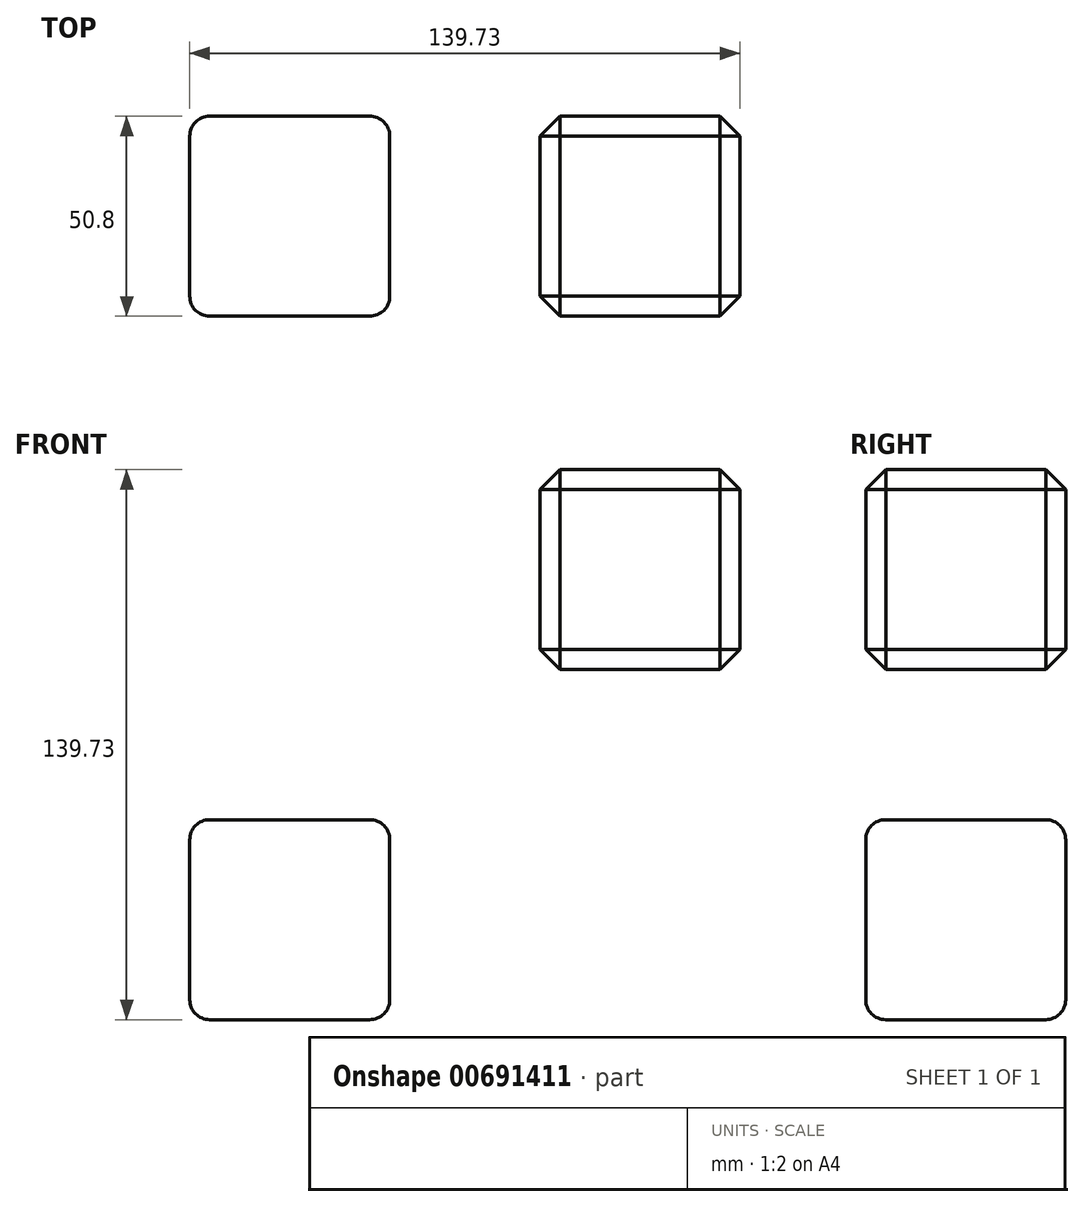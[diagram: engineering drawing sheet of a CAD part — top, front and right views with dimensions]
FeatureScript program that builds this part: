
annotation { "Feature Type Name" : "Feature", "Feature Type Description" : "" }
export const myFeature = defineFeature(function(context is Context, id is Id, definition is map)
    precondition{}
    {
        {
            var Q0;
            Q0=qCreatedBy(makeId("Front.planeOp"),FACE);
            var sketch = newSketch(context, id + "F0", { "sketchPlane" : qUnion([Q0])});
            skLineSegment(sketch, "E0.bottom", {"start": v(-25.4, 25.4) * mm, "end": v(25.4, 25.4) * mm});
            skLineSegment(sketch, "E0.top", {"start": v(-25.4, -25.4) * mm, "end": v(25.4, -25.4) * mm});
            skLineSegment(sketch, "E0.left", {"start": v(-25.4, 25.4) * mm, "end": v(-25.4, -25.4) * mm});
            skLineSegment(sketch, "E0.right", {"start": v(25.4, 25.4) * mm, "end": v(25.4, -25.4) * mm});
            skPoint(sketch, "E0.middle", {"position": v(0, 0) * mm});
            skLineSegment(sketch, "E1.bottom", {"start": v(63.53, 63.53) * mm, "end": v(114.33, 63.53) * mm});
            skLineSegment(sketch, "E1.top", {"start": v(63.53, 114.33) * mm, "end": v(114.33, 114.33) * mm});
            skLineSegment(sketch, "E1.left", {"start": v(63.53, 63.53) * mm, "end": v(63.53, 114.33) * mm});
            skLineSegment(sketch, "E1.right", {"start": v(114.33, 63.53) * mm, "end": v(114.33, 114.33) * mm});
            skLineSegment(sketch, "E2.0", {"start": v(63.53, 107.98) * mm, "end": v(38.13, 107.98) * mm});
            skArc(sketch, "E2.1", {"start": v(-19.05, 50.8) * mm, "mid": v(-2.3, 91.23) * mm, "end": v(38.13, 107.98) * mm});
            skLineSegment(sketch, "E2.2", {"start": v(-19.05, 25.4) * mm, "end": v(-19.05, 50.8) * mm});
            skLineSegment(sketch, "E3.0", {"start": v(38.13, 69.88) * mm, "end": v(63.53, 69.88) * mm});
            skArc(sketch, "E3.1", {"start": v(19.05, 50.8) * mm, "mid": v(24.64, 64.3) * mm, "end": v(38.13, 69.88) * mm});
            skLineSegment(sketch, "E3.2", {"start": v(19.05, 25.4) * mm, "end": v(19.05, 50.8) * mm});
            skSolve(sketch);
        }
        {
            var Q0;
            {var subQ3=sQuery(id+"F0.wireOp",EDGE,"E1.bottom");Q0=makeQuery(id+"F0.imprint","IMPRINT",FACE,{"disambiguationData":[TD([[makeQuery(id+"F0.imprint","IMPRINT",EDGE,{"derivedFrom":subQ3}),1.0]])]});}
            var Q1;
            Q1=makeQuery(id+"F0.imprint","IMPRINT",FACE,{"disambiguationData":[TD([[makeQuery(id+"F0.imprint","IMPRINT",EDGE,{"derivedFrom":sQuery(id+"F0.wireOp",EDGE,"E0.top")}),1.0]])]});
            extrude(context, id + "F1", {"entities" : qUnion([Q0, Q1]), "endBound" : BoundingType.SYMMETRIC, "depth" : 50.8 * mm, "offsetDistance" : 25.4 * mm});
        }
        {
            var Q0;
            Q0=makeQuery(id+"F1.opExtrude","CAP_EDGE",EDGE,{"disambiguationData":[OSD([sQuery(id+"F0.wireOp",EDGE,"E0.bottom")])],"isStart":false});
            var Q1;
            Q1=makeQuery(id+"F1.opExtrude","CAP_EDGE",EDGE,{"disambiguationData":[OSD([sQuery(id+"F0.wireOp",EDGE,"E0.right")])],"isStart":false});
            var Q2;
            Q2=makeQuery(id+"F1.opExtrude","SWEPT_EDGE",EDGE,{"disambiguationData":[OSD([sQuery(id+"F0.wireOp",EDGE,"E0.bottom"),sQuery(id+"F0.wireOp",EDGE,"E0.right")])]});
            var Q3;
            Q3=makeQuery(id+"F1.opExtrude","SWEPT_EDGE",EDGE,{"disambiguationData":[OSD([sQuery(id+"F0.wireOp",EDGE,"E0.bottom"),sQuery(id+"F0.wireOp",EDGE,"E0.left")])]});
            var Q4;
            Q4=makeQuery(id+"F1.opExtrude","CAP_FACE",FACE,{"disambiguationData":[OSD([sQuery(id+"F0.wireOp",EDGE,"E0.bottom"),sQuery(id+"F0.wireOp",EDGE,"E0.top"),sQuery(id+"F0.wireOp",EDGE,"E0.left"),sQuery(id+"F0.wireOp",EDGE,"E0.right")])],"isStart":false});
            var Q5;
            Q5=makeQuery(id+"F1.opExtrude","SWEPT_FACE",FACE,{"disambiguationData":[OSD([sQuery(id+"F0.wireOp",EDGE,"E0.right")])]});
            var Q6;
            Q6=makeQuery(id+"F1.opExtrude","SWEPT_FACE",FACE,{"disambiguationData":[OSD([sQuery(id+"F0.wireOp",EDGE,"E0.left")])]});
            var Q7;
            Q7=makeQuery(id+"F1.opExtrude","CAP_FACE",FACE,{"disambiguationData":[OSD([sQuery(id+"F0.wireOp",EDGE,"E0.bottom"),sQuery(id+"F0.wireOp",EDGE,"E0.top"),sQuery(id+"F0.wireOp",EDGE,"E0.left"),sQuery(id+"F0.wireOp",EDGE,"E0.right")])],"isStart":true});
            fillet(context, id + "F2", {"entities" : qUnion([Q0, Q1, Q2, Q3, Q4, Q5, Q6, Q7]), "radius" : 5.08 * mm, "tangentPropagation" : true, "allowEdgeOverflow" : false});
        }
        {
            var Q0;
            Q0=makeQuery(id+"F1.opExtrude","CAP_FACE",FACE,{"disambiguationData":[OSD([sQuery(id+"F0.wireOp",EDGE,"E1.bottom"),sQuery(id+"F0.wireOp",EDGE,"E1.top"),sQuery(id+"F0.wireOp",EDGE,"E1.left"),sQuery(id+"F0.wireOp",EDGE,"E1.right")])],"isStart":true});
            var Q1;
            Q1=makeQuery(id+"F1.opExtrude","SWEPT_EDGE",EDGE,{"disambiguationData":[OSD([sQuery(id+"F0.wireOp",EDGE,"E1.top"),sQuery(id+"F0.wireOp",EDGE,"E1.left")])]});
            var Q2;
            Q2=makeQuery(id+"F1.opExtrude","SWEPT_FACE",FACE,{"disambiguationData":[OSD([sQuery(id+"F0.wireOp",EDGE,"E1.right")])]});
            var Q3;
            Q3=makeQuery(id+"F1.opExtrude","CAP_FACE",FACE,{"disambiguationData":[OSD([sQuery(id+"F0.wireOp",EDGE,"E1.bottom"),sQuery(id+"F0.wireOp",EDGE,"E1.top"),sQuery(id+"F0.wireOp",EDGE,"E1.left"),sQuery(id+"F0.wireOp",EDGE,"E1.right")])],"isStart":false});
            var Q4;
            Q4=makeQuery(id+"F1.opExtrude","SWEPT_FACE",FACE,{"disambiguationData":[OSD([sQuery(id+"F0.wireOp",EDGE,"E1.bottom")])]});
            chamfer(context, id + "F3", {"entities" : qUnion([Q0, Q1, Q2, Q3, Q4]), "width" : 5.08 * mm, "tangentPropagation" : true});
        }
    });
